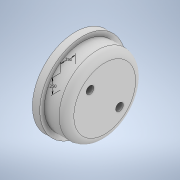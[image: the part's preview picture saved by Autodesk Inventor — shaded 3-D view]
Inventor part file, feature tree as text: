
AUTODESK INVENTOR PART (.ipt)
format: ipt  version: 2020 (Build 240168000, 168)  size: 147,968 bytes
history: native  units: in
note: dims shown in document units (in); Inventor stores cm internally (conversion verified against a paired STEP export)
features: sketch x2, hole x2, revolve x1, pattern_circular x1, fillet x1
ambient origin geometry x8: Origin, YZ Plane, XZ Plane, XY Plane, X Axis, Y Axis, Z Axis, Center Point
bodies: Solid1 (feature_tree)
feature tree (7):
  revolve  "Revolution1"  [1 undecoded]
  sketch  "Sketch2"  dims[d2=0.375in d3=0.6496in d4=90.0deg d5=0.25in d6=0.25in d7=0.213in d8=0.25in d9=0.375in d10=0.25in d11=0.5635in d12=0.25in d13=0.0in d14=0.13in d15=0.25in d16=0.119in d17=0.25in d18=0.5635in d19=0.5in d20=0.8108in d21=0.7874in d22=360.0deg d24=0.125in]
  hole  "Hole1"  [1 undecoded]
  hole  "Hole2"  [1 undecoded]
  pattern_circular  "Circular Pattern1"  [2 undecoded]
  fillet  "Fillet1"  Radius=0.25in
  sketch  "Sketch1"  dims[d0=0.125in d1=0.7283in]
note: 5 required parameter values undecoded (feature->parameter linkage not recoverable at this tier; creation-order binding heuristic only, values carry confidence <= 0.55)